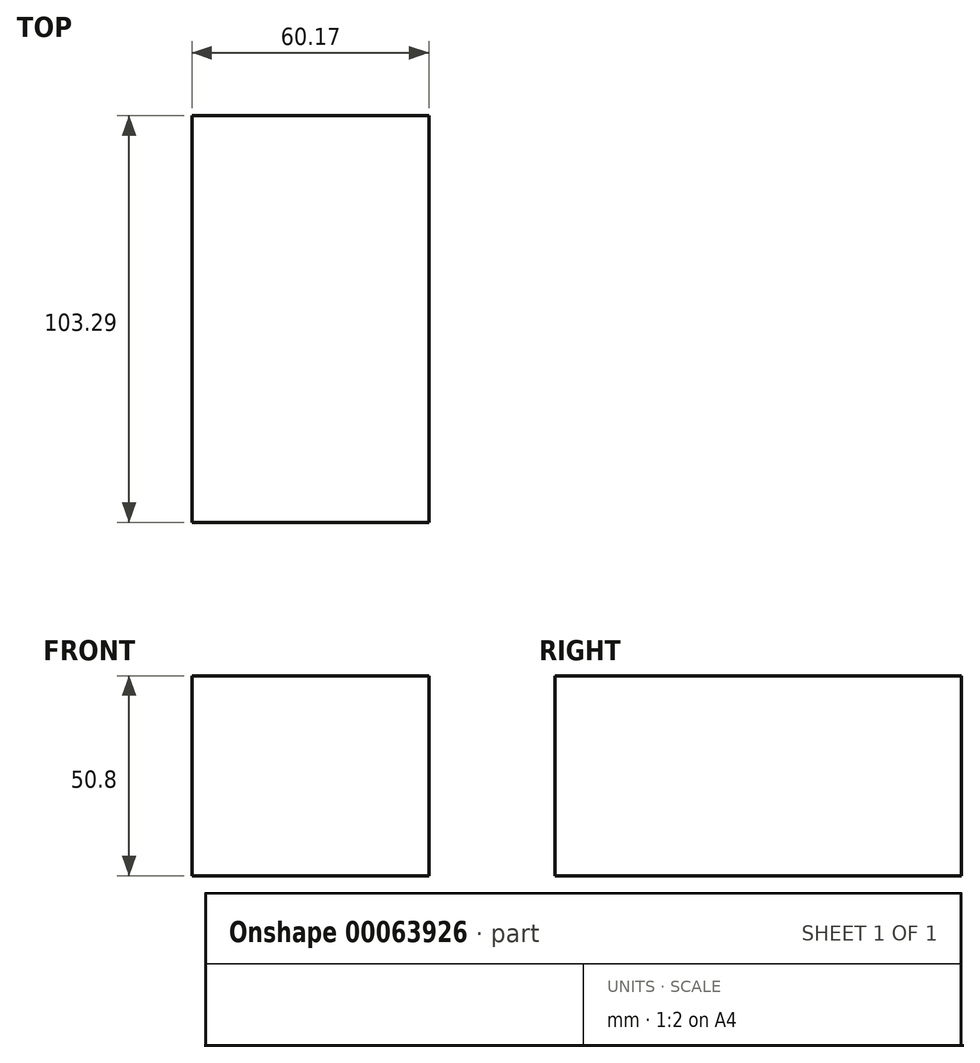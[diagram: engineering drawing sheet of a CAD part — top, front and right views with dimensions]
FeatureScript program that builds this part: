
annotation { "Feature Type Name" : "Feature", "Feature Type Description" : "" }
export const myFeature = defineFeature(function(context is Context, id is Id, definition is map)
    precondition{}
    {
        {
            var Q0;
            Q0=qCreatedBy(makeId("Top.planeOp"),FACE);
            var sketch = newSketch(context, id + "F0", { "sketchPlane" : qUnion([Q0])});
            skLineSegment(sketch, "E0.bottom", {"start": v(-97.55, 57.86) * mm, "end": v(-37.38, 57.86) * mm});
            skLineSegment(sketch, "E0.top", {"start": v(-97.55, -45.43) * mm, "end": v(-37.38, -45.43) * mm});
            skLineSegment(sketch, "E0.left", {"start": v(-97.55, 57.86) * mm, "end": v(-97.55, -45.43) * mm});
            skLineSegment(sketch, "E0.right", {"start": v(-37.38, 57.86) * mm, "end": v(-37.38, -45.43) * mm});
            skLineSegment(sketch, "E1.bottom", {"start": v(-24.1, 158.36) * mm, "end": v(-37.38, 158.36) * mm});
            skLineSegment(sketch, "E1.top", {"start": v(-24.1, 41.24) * mm, "end": v(-37.38, 41.24) * mm});
            skLineSegment(sketch, "E1.left", {"start": v(-24.1, 158.36) * mm, "end": v(-24.1, 41.24) * mm});
            skLineSegment(sketch, "E1.right", {"start": v(-37.38, 158.36) * mm, "end": v(-37.38, 41.24) * mm});
            skSolve(sketch);
        }
        {
            var Q0;
            Q0=sQuery(id+"F0.wireOp",EDGE,"E1.left");
            var Q1;
            Q1=sQuery(id+"F0.wireOp",EDGE,"E1.bottom");
            var Q2;
            Q2=sQuery(id+"F0.wireOp",EDGE,"E1.top");
            var Q3;
            Q3=sQuery(id+"F0.wireOp",EDGE,"E1.right");
            extrude(context, id + "F2", {"bodyType" : ToolBodyType.SURFACE, "surfaceEntities" : qUnion([Q0, Q1, Q2, Q3]), "depth" : 50.8 * mm});
        }
        {
            var Q0;
            {var subQ2=sQuery(id+"F0.wireOp",EDGE,"E0.bottom");Q0=makeQuery(id+"F0.imprint","IMPRINT",FACE,{"disambiguationData":[TD([[makeQuery(id+"F0.imprint","IMPRINT",EDGE,{"derivedFrom":subQ2}),-1.0]])]});}
            extrude(context, id + "F1", {"entities" : qUnion([Q0]), "depth" : 50.8 * mm});
        }
    });
